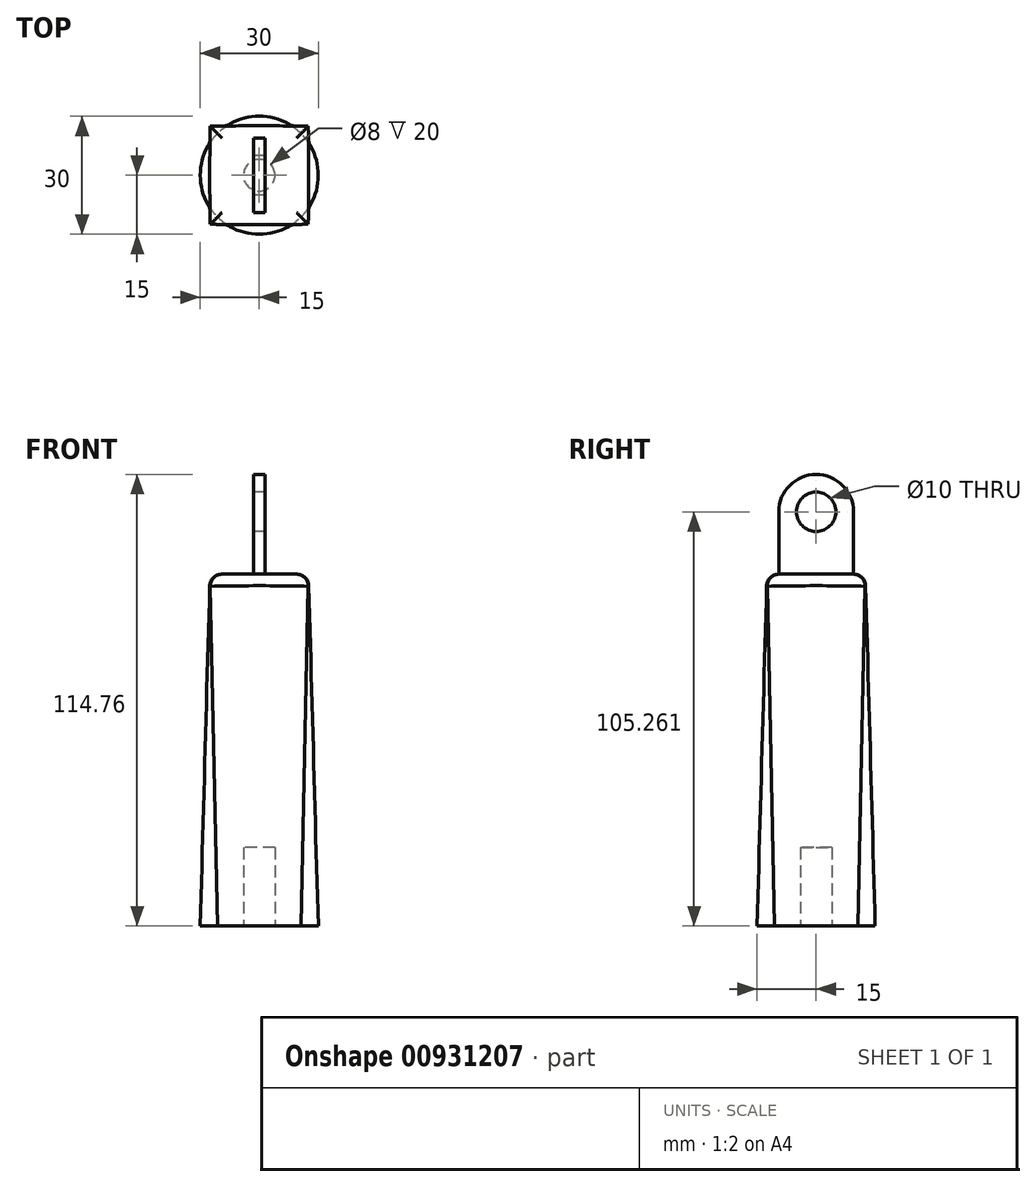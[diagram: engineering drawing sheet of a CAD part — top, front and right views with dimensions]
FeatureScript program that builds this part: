
annotation { "Feature Type Name" : "Feature", "Feature Type Description" : "" }
export const myFeature = defineFeature(function(context is Context, id is Id, definition is map)
    precondition{}
    {
        {
            var Q0;
            Q0=qCreatedBy(makeId("Top.planeOp"),FACE);
            var sketch = newSketch(context, id + "F0", { "sketchPlane" : qUnion([Q0])});
            skCircle(sketch, "E0", {"center": v(0, 0) * mm, "radius": 15 * mm});
            skSolve(sketch);
        }
        {
            var Q0;
            Q0=qCreatedBy(makeId("Top.planeOp"),FACE);
            cPlane(context, id + "F1", {"entities" : qUnion([Q0]), "cplaneType" : CPlaneType.OFFSET, "offset" : 89.4 * mm, "width" : 150 * mm, "height" : 150 * mm});
        }
        {
            var Q0;
            Q0=qCreatedBy(id+"F1.planeOp",FACE);
            var sketch = newSketch(context, id + "F2", { "sketchPlane" : qUnion([Q0])});
            skLineSegment(sketch, "E1.bottom", {"start": v(12.5, -12.5) * mm, "end": v(-12.5, -12.5) * mm});
            skLineSegment(sketch, "E1.top", {"start": v(12.5, 12.5) * mm, "end": v(-12.5, 12.5) * mm});
            skLineSegment(sketch, "E1.left", {"start": v(12.5, -12.5) * mm, "end": v(12.5, 12.5) * mm});
            skLineSegment(sketch, "E1.right", {"start": v(-12.5, -12.5) * mm, "end": v(-12.5, 12.5) * mm});
            skPoint(sketch, "E1.middle", {"position": v(0, 0) * mm});
            skSolve(sketch);
        }
        {
            var Q0;
            Q0=makeQuery(id+"F0.imprint","IMPRINT",FACE,{"disambiguationData":[TD([[makeQuery(id+"F0.imprint","IMPRINT",EDGE,{"derivedFrom":sQuery(id+"F0.wireOp",EDGE,"E0")}),1.0]])]});
            var Q1;
            Q1=makeQuery(id+"F2.imprint","IMPRINT",FACE,{"disambiguationData":[TD([[makeQuery(id+"F2.imprint","IMPRINT",EDGE,{"derivedFrom":sQuery(id+"F2.wireOp",EDGE,"E1.bottom")}),-1.0]])]});
            loft(context, id + "F3", {"sheetProfilesArray" : [{ "sheetProfileEntities" : qUnion([Q0]) }, { "sheetProfileEntities" : qUnion([Q1]) }]});
        }
        {
            var Q0;
            Q0=makeQuery(id+"F3.opLoft","MID_CAP_EDGE",EDGE,{"disambiguationData":[OSD([sQuery(id+"F2.wireOp",EDGE,"E1.bottom"),sQuery(id+"F2.wireOp",EDGE,"E1.top"),sQuery(id+"F2.wireOp",EDGE,"E1.left")])],"capPos":1.0});
            var Q1;
            Q1=makeQuery(id+"F3.opLoft","MID_CAP_EDGE",EDGE,{"disambiguationData":[OSD([sQuery(id+"F2.wireOp",EDGE,"E1.top"),sQuery(id+"F2.wireOp",EDGE,"E1.left"),sQuery(id+"F2.wireOp",EDGE,"E1.right")])],"capPos":1.0});
            var Q2;
            Q2=makeQuery(id+"F3.opLoft","MID_CAP_EDGE",EDGE,{"disambiguationData":[OSD([sQuery(id+"F2.wireOp",EDGE,"E1.bottom"),sQuery(id+"F2.wireOp",EDGE,"E1.top"),sQuery(id+"F2.wireOp",EDGE,"E1.right")])],"capPos":1.0});
            var Q3;
            Q3=makeQuery(id+"F3.opLoft","MID_CAP_EDGE",EDGE,{"disambiguationData":[OSD([sQuery(id+"F2.wireOp",EDGE,"E1.bottom"),sQuery(id+"F2.wireOp",EDGE,"E1.left"),sQuery(id+"F2.wireOp",EDGE,"E1.right")])],"capPos":1.0});
            fillet(context, id + "F4", {"entities" : qUnion([Q0, Q1, Q2, Q3]), "radius" : 3 * mm, "tangentPropagation" : true, "allowEdgeOverflow" : false});
        }
        {
            var Q0;
            Q0=qCreatedBy(makeId("Right.planeOp"),FACE);
            var sketch = newSketch(context, id + "F5", { "sketchPlane" : qUnion([Q0])});
            skCircle(sketch, "E2", {"center": v(0, 105.26) * mm, "radius": 5 * mm});
            skCircle(sketch, "E3", {"center": v(0, 105.26) * mm, "radius": 9.5 * mm});
            skLineSegment(sketch, "E4", {"start": v(0, 105.26) * mm, "end": v(0, 65.96) * mm, "construction": true});
            skLineSegment(sketch, "E5", {"start": v(9.5, 105.26) * mm, "end": v(9.5, 83.35) * mm});
            skLineSegment(sketch, "E6.MirrorCS", {"start": v(-9.5, 105.26) * mm, "end": v(-9.5, 83.35) * mm});
            skLineSegment(sketch, "E7", {"start": v(-9.5, 83.35) * mm, "end": v(9.5, 83.35) * mm});
            skSolve(sketch);
        }
        {
            var Q0;
            {var subQ0=sQuery(id+"F5.wireOp",EDGE,"E5");Q0=makeQuery(id+"F5.imprint","IMPRINT",FACE,{"disambiguationData":[TD([[makeQuery(id+"F5.imprint","IMPRINT",EDGE,{"derivedFrom":subQ0}),-1.0]])]});}
            var Q1;
            Q1=makeQuery(id+"F5.imprint","IMPRINT",FACE,{"disambiguationData":[TD([[makeQuery(id+"F5.imprint","IMPRINT",EDGE,{"derivedFrom":sQuery(id+"F5.wireOp",EDGE,"E2")}),-1.0]])]});
            extrude(context, id + "F6", {"entities" : qUnion([Q0, Q1]), "operationType" : NewBodyOperationType.ADD, "endBound" : BoundingType.SYMMETRIC, "depth" : 3 * mm, "offsetDistance" : 25 * mm});
        }
        {
            var Q0;
            Q0=qCreatedBy(makeId("Top.planeOp"),FACE);
            var sketch = newSketch(context, id + "F7", { "sketchPlane" : qUnion([Q0])});
            skCircle(sketch, "E8", {"center": v(0, 0) * mm, "radius": 4 * mm});
            skSolve(sketch);
        }
        {
            var Q0;
            Q0=makeQuery(id+"F7.imprint","IMPRINT",FACE,{"disambiguationData":[TD([[makeQuery(id+"F7.imprint","IMPRINT",EDGE,{"derivedFrom":sQuery(id+"F7.wireOp",EDGE,"E8")}),1.0]])]});
            extrude(context, id + "F8", {"entities" : qUnion([Q0]), "operationType" : NewBodyOperationType.REMOVE, "depth" : 20 * mm, "offsetDistance" : 25 * mm});
        }
    });
